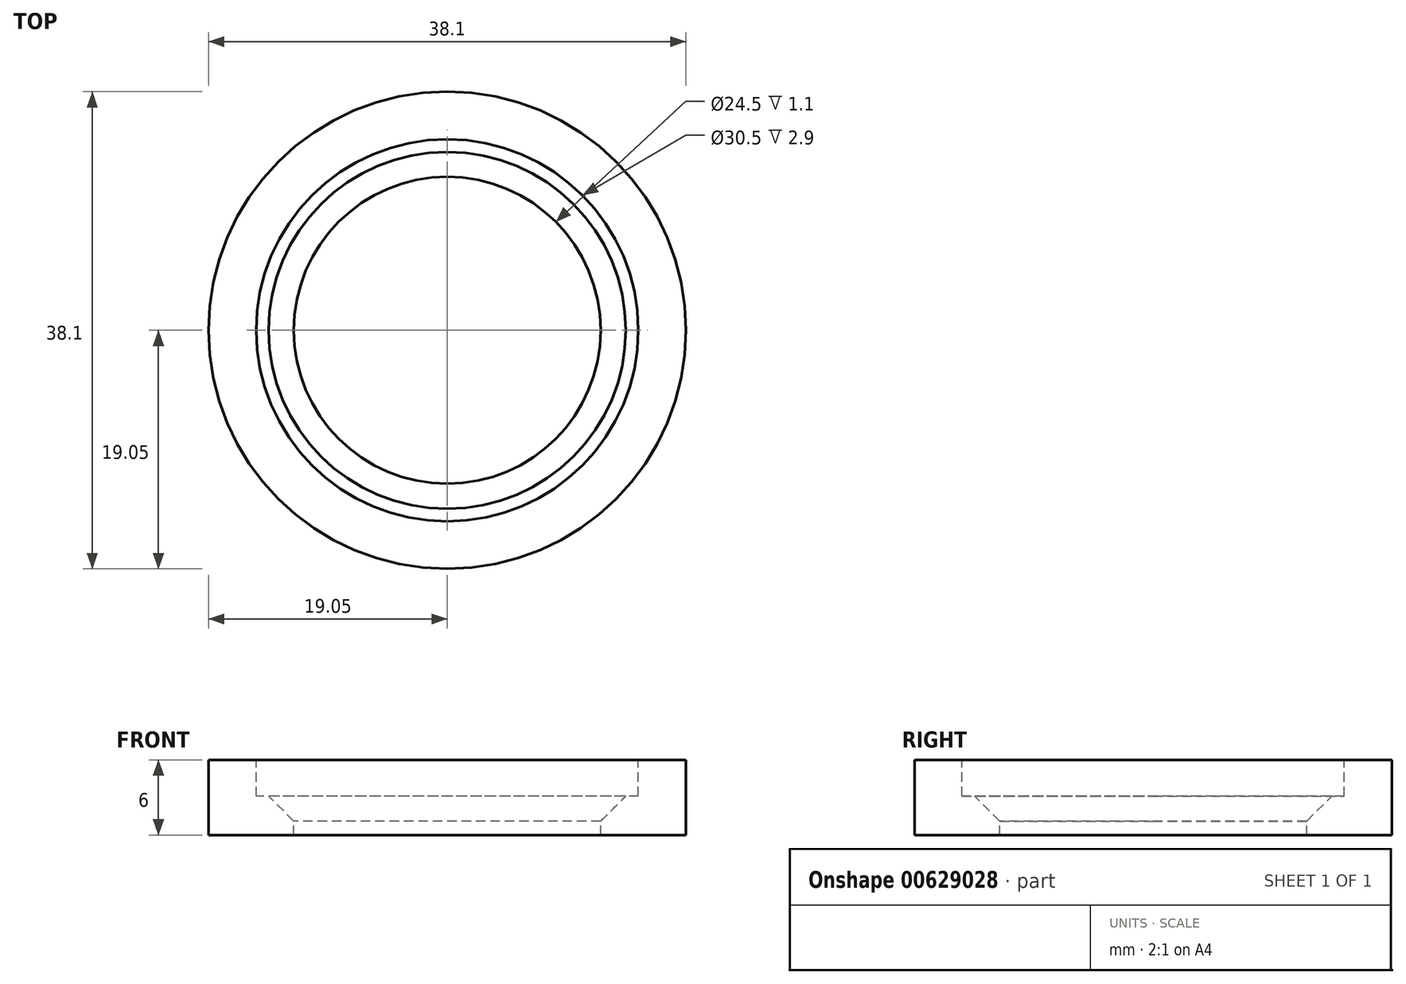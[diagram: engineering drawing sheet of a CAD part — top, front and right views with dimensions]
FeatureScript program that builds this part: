
annotation { "Feature Type Name" : "Feature", "Feature Type Description" : "" }
export const myFeature = defineFeature(function(context is Context, id is Id, definition is map)
    precondition{}
    {
        {
            var Q0;
            Q0=qCreatedBy(makeId("Top.planeOp"),FACE);
            var sketch = newSketch(context, id + "F0", { "sketchPlane" : qUnion([Q0])});
            skCircle(sketch, "E0", {"center": v(0, 0) * mm, "radius": 19.05 * mm});
            skSolve(sketch);
        }
        {
            var Q0;
            Q0=qSketchRegion(id+"F0",true);
            var Q1;
            Q1 = qSketchRegion(id + "F2", true);
            extrude(context, id + "F1", {"entities" : qUnion([Q0, Q1]), "depth" : 6 * mm, "offsetDistance" : 25 * mm});
        }
        {
            var Q0;
            Q0=makeQuery(id+"F1.opExtrude","CAP_FACE",FACE,{"disambiguationData":[OSD([sQuery(id+"F0.wireOp",EDGE,"E0")])],"isStart":false});
            var sketch = newSketch(context, id + "F2", { "sketchPlane" : qUnion([Q0])});
            skCircle(sketch, "E1", {"center": v(0, 0) * mm, "radius": 12.25 * mm});
            skSolve(sketch);
        }
        {
            var Q0;
            Q0 = qSketchRegion(id + "F2", true);
            extrude(context, id + "F3", {"entities" : qUnion([Q0]), "operationType" : NewBodyOperationType.REMOVE, "oppositeDirection" : true, "depth" : 6 * mm, "offsetDistance" : 25 * mm});
        }
        {
            var Q0;
            Q0=makeQuery(id+"F1.opExtrude","CAP_FACE",FACE,{"disambiguationData":[OSD([sQuery(id+"F0.wireOp",EDGE,"E0")])],"isStart":false});
            var sketch = newSketch(context, id + "F4", { "sketchPlane" : qUnion([Q0])});
            skCircle(sketch, "E2", {"center": v(0, 0) * mm, "radius": 15.25 * mm});
            skSolve(sketch);
        }
        {
            var Q0;
            Q0 = qSketchRegion(id + "F4", true);
            extrude(context, id + "F5", {"entities" : qUnion([Q0]), "operationType" : NewBodyOperationType.REMOVE, "oppositeDirection" : true, "depth" : 2.9 * mm, "offsetDistance" : 25 * mm});
        }
        {
            var Q0;
            Q0=makeQuery(id+"F5.boolean.opBoolean","INTERSECT",EDGE,{"derivedFrom":[makeQuery(id+"F3.boolean.opBoolean","COPY",FACE,{"derivedFrom":makeQuery(id+"F3.opExtrude","SWEPT_FACE",FACE,{"disambiguationData":[OSD([sQuery(id+"F2.wireOp",EDGE,"E1")])]})}),makeQuery(id+"F5.opExtrude","CAP_FACE",FACE,{"disambiguationData":[OSD([sQuery(id+"F4.wireOp",EDGE,"E2")])],"isStart":false})]});
            chamfer(context, id + "F6", {"entities" : qUnion([Q0]), "width" : 2 * mm, "tangentPropagation" : true});
        }
    });
